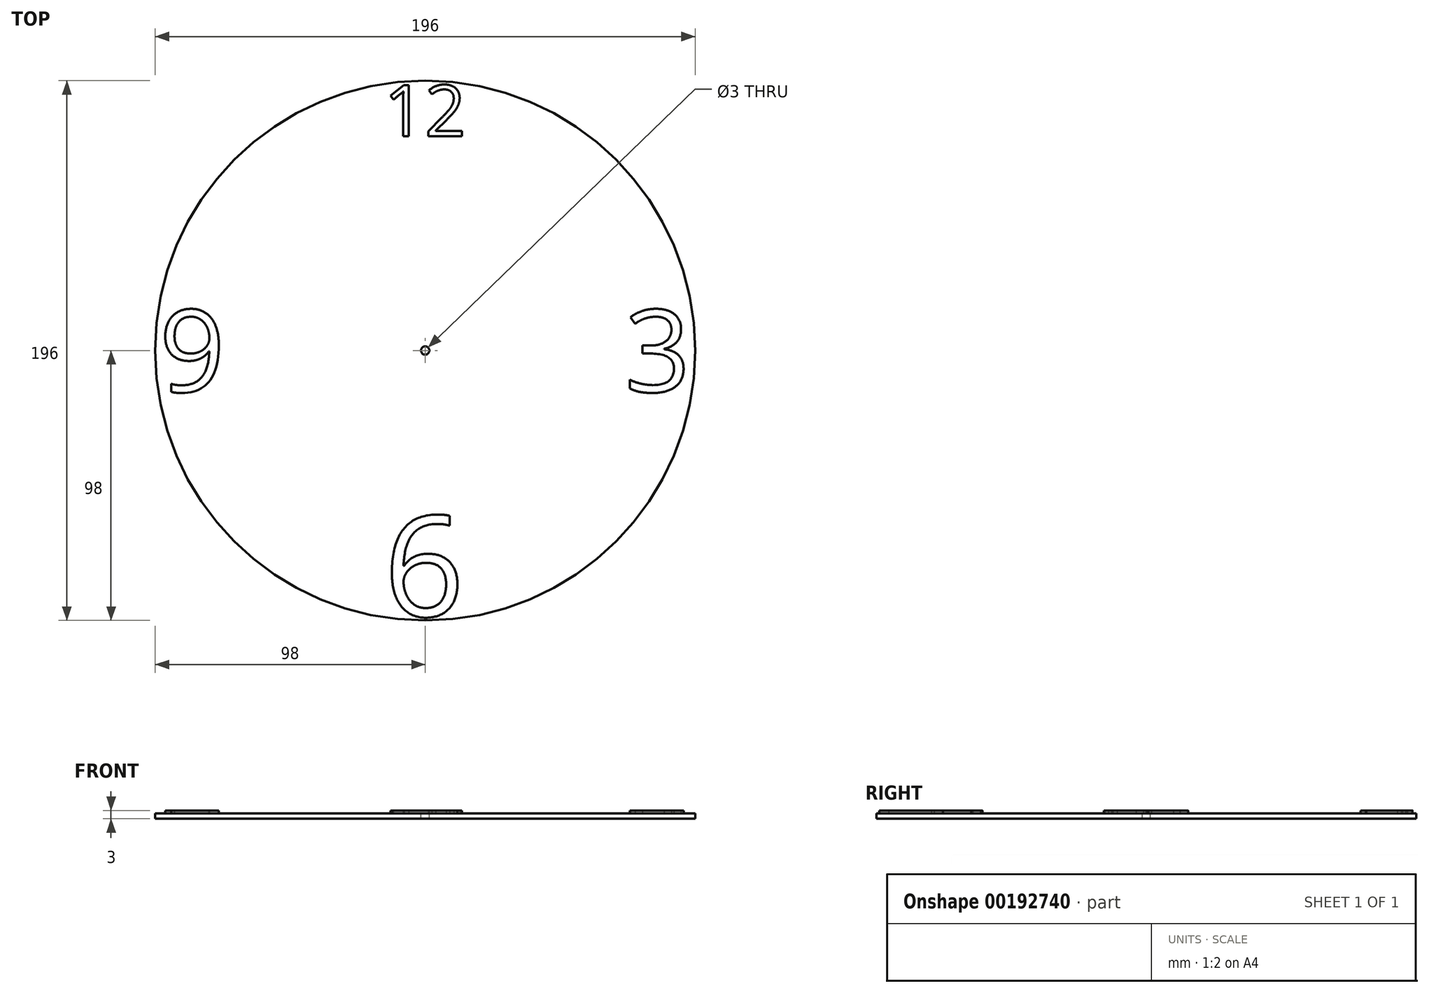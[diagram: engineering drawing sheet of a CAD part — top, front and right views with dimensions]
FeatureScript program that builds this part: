
annotation { "Feature Type Name" : "Feature", "Feature Type Description" : "" }
export const myFeature = defineFeature(function(context is Context, id is Id, definition is map)
    precondition{}
    {
        {
            var Q0;
            Q0=qCreatedBy(makeId("Top.planeOp"),FACE);
            var sketch = newSketch(context, id + "F0", { "sketchPlane" : qUnion([Q0])});
            skCircle(sketch, "E0", {"center": v(0, 0) * mm, "radius": 98 * mm});
            skSolve(sketch);
        }
        {
            var Q0;
            Q0 = qSketchRegion(id + "F0", true);
            extrude(context, id + "F1", {"entities" : qUnion([Q0]), "depth" : 2 * mm});
        }
        {
            var Q0;
            Q0=makeQuery(id+"F1.opExtrude","CAP_FACE",FACE,{"disambiguationData":[OSD([sQuery(id+"F0.wireOp",EDGE,"E0")])],"isStart":false});
            var sketch = newSketch(context, id + "F2", { "sketchPlane" : qUnion([Q0])});
            skText(sketch, "E1", { "text": "12\n", "fontName": "OpenSans-Regular.ttf"});
            skText(sketch, "E2", { "text": "6", "fontName": "OpenSans-Regular.ttf"});
            skText(sketch, "E3", { "text": "3", "fontName": "OpenSans-Regular.ttf"});
            skLineSegment(sketch, "E4", {"start": v(95, 0) * mm, "end": v(70.92, 0) * mm, "construction": true});
            skText(sketch, "E5", { "text": "9", "fontName": "OpenSans-Regular.ttf"});
            skLineSegment(sketch, "E6", {"start": v(-70.7, 0) * mm, "end": v(-95, 0) * mm, "construction": true});
            const initialGuessF2  = {"E1": [-0.015, 0.0778, 1, 0, 0.0187], "E2": [-0.015, -0.0965, 1, 0, 0.03675], "E3": [0.07242, -0.015, 1, 0, 0.03], "E5": [-0.0965, -0.015, 1, 0, 0.03]};
            skSetInitialGuess(sketch, initialGuessF2);
            skSolve(sketch);
        }
        {
            var Q0;
            Q0 = qSketchRegion(id + "F2", true);
            extrude(context, id + "F3", {"entities" : qUnion([Q0]), "operationType" : NewBodyOperationType.ADD, "depth" : 1 * mm});
        }
        {
            var Q0;
            {var subQ0=sQuery(id+"F0.wireOp",EDGE,"E0");Q0=makeQuery(id+"F3.boolean.opBoolean","SPLIT",FACE,{"disambiguationData":[TD([makeQuery(id+"F1.opExtrude","SWEPT_FACE",FACE,{"disambiguationData":[OSD([subQ0])]})])],"derivedFrom":makeQuery(id+"F1.opExtrude","CAP_FACE",FACE,{"disambiguationData":[OSD([subQ0])],"isStart":false})});}
            var sketch = newSketch(context, id + "F4", { "sketchPlane" : qUnion([Q0])});
            skCircle(sketch, "E7", {"center": v(0, 0) * mm, "radius": 1.5 * mm});
            skSolve(sketch);
        }
        {
            var Q0;
            Q0 = qSketchRegion(id + "F4", true);
            extrude(context, id + "F5", {"entities" : qUnion([Q0]), "operationType" : NewBodyOperationType.REMOVE, "oppositeDirection" : true, "depth" : 4 * mm});
        }
    });
